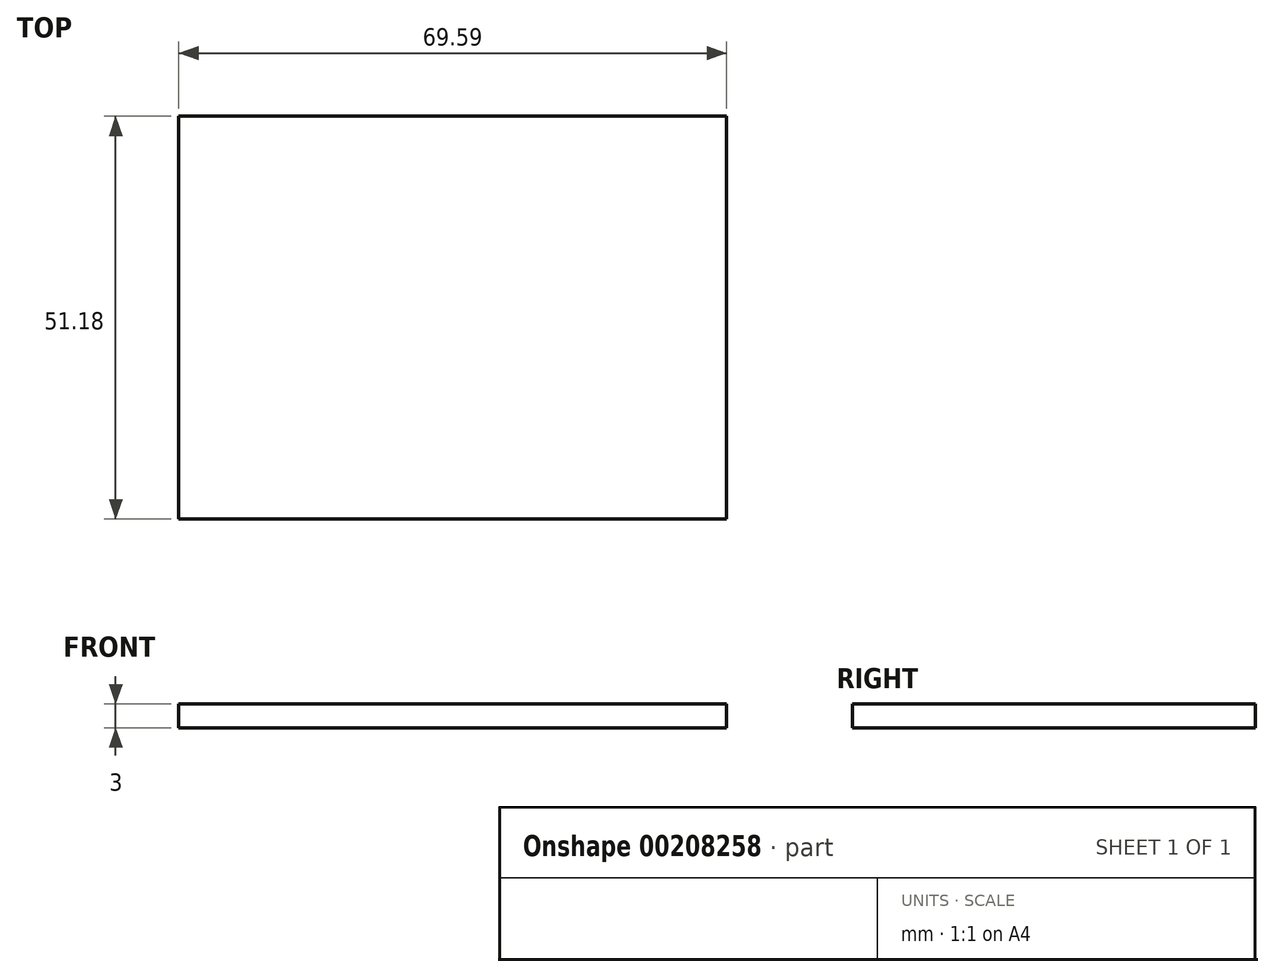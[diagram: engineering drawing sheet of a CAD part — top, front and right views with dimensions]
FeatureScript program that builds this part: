
annotation { "Feature Type Name" : "Feature", "Feature Type Description" : "" }
export const myFeature = defineFeature(function(context is Context, id is Id, definition is map)
    precondition{}
    {
        {
            var Q0;
            Q0=qCreatedBy(makeId("Top.planeOp"),FACE);
            var sketch = newSketch(context, id + "F0", { "sketchPlane" : qUnion([Q0])});
            skLineSegment(sketch, "E0.bottom", {"start": v(-55.71, 51.18) * mm, "end": v(13.88, 51.18) * mm});
            skLineSegment(sketch, "E0.top", {"start": v(-55.71, 0) * mm, "end": v(13.88, 0) * mm});
            skLineSegment(sketch, "E0.left", {"start": v(-55.71, 51.18) * mm, "end": v(-55.71, 0) * mm});
            skLineSegment(sketch, "E0.right", {"start": v(13.88, 51.18) * mm, "end": v(13.88, 0) * mm});
            skSolve(sketch);
        }
        {
            var Q0;
            Q0=makeQuery(id+"F0.imprint","IMPRINT",FACE,{"disambiguationData":[TD([[makeQuery(id+"F0.imprint","IMPRINT",EDGE,{"derivedFrom":sQuery(id+"F0.wireOp",EDGE,"E0.bottom")}),-1.0]])]});
            extrude(context, id + "F1", {"entities" : qUnion([Q0]), "depth" : 3 * mm});
        }
    });
